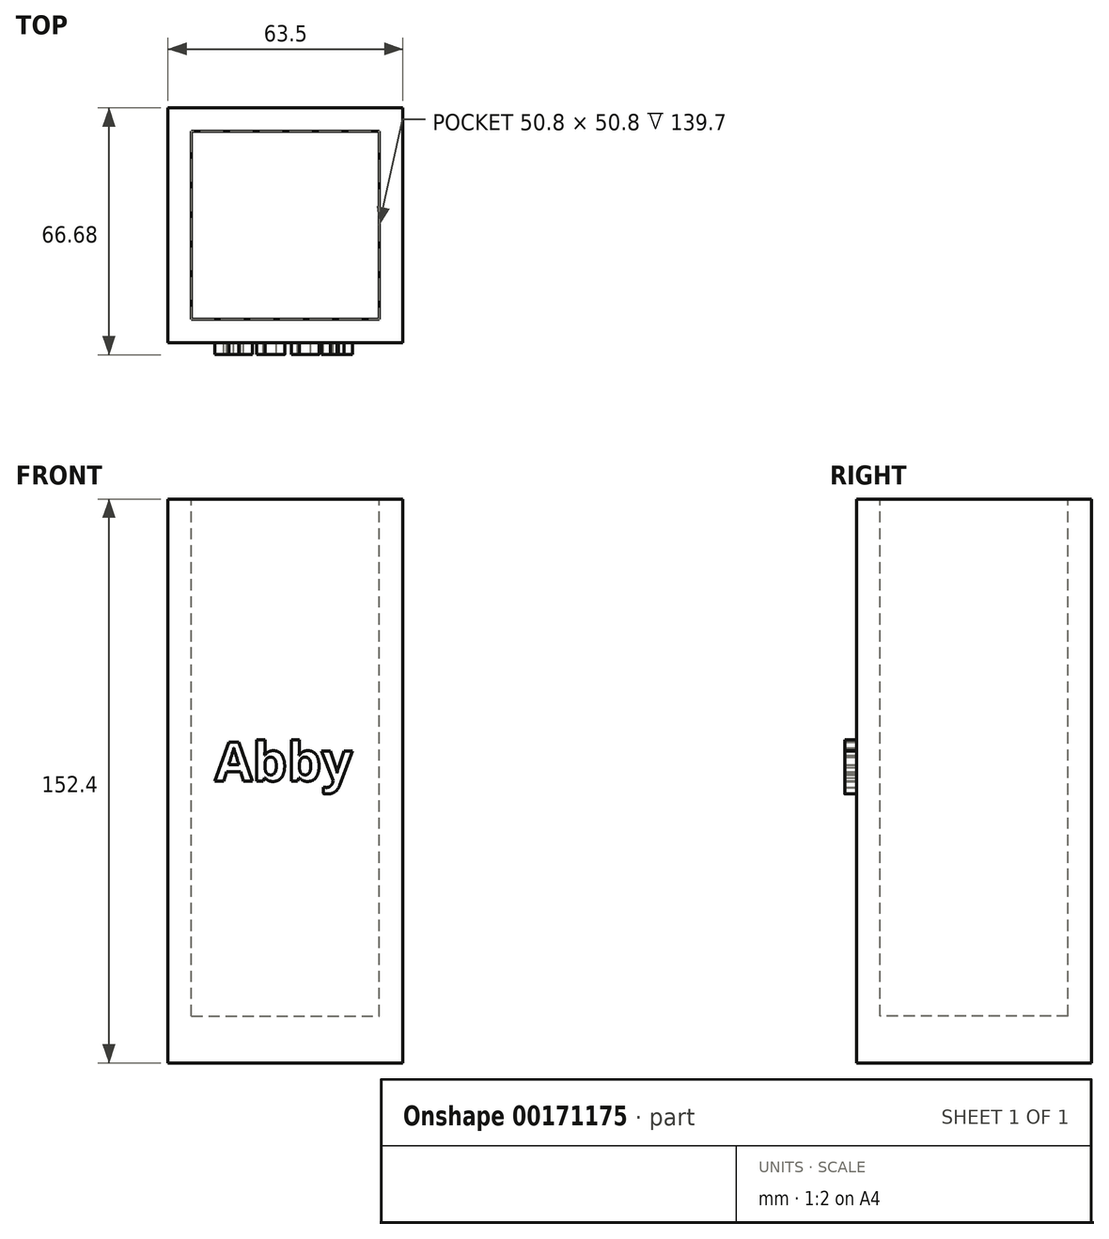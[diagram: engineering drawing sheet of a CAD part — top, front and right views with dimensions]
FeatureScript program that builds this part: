
annotation { "Feature Type Name" : "Feature", "Feature Type Description" : "" }
export const myFeature = defineFeature(function(context is Context, id is Id, definition is map)
    precondition{}
    {
        {
            var Q0;
            Q0=qCreatedBy(makeId("Front.planeOp"),FACE);
            var sketch = newSketch(context, id + "F0", { "sketchPlane" : qUnion([Q0])});
            skLineSegment(sketch, "E0.bottom", {"start": v(-32.8, 125.6) * mm, "end": v(30.7, 125.6) * mm});
            skLineSegment(sketch, "E0.top", {"start": v(-32.8, -26.8) * mm, "end": v(30.7, -26.8) * mm});
            skLineSegment(sketch, "E0.left", {"start": v(-32.8, 125.6) * mm, "end": v(-32.8, -26.8) * mm});
            skLineSegment(sketch, "E0.right", {"start": v(30.7, 125.6) * mm, "end": v(30.7, -26.8) * mm});
            skSolve(sketch);
        }
        {
            var Q0;
            Q0 = qSketchRegion(id + "F0", true);
            extrude(context, id + "F1", {"entities" : qUnion([Q0]), "depth" : 63.5 * mm});
        }
        {
            var Q0;
            Q0=makeQuery(id+"F1.opExtrude","SWEPT_FACE",FACE,{"disambiguationData":[OSD([sQuery(id+"F0.wireOp",EDGE,"E0.bottom")])]});
            var sketch = newSketch(context, id + "F2", { "sketchPlane" : qUnion([Q0])});
            skLineSegment(sketch, "E1.bottom", {"start": v(-26.44, -6.35) * mm, "end": v(24.36, -6.35) * mm});
            skLineSegment(sketch, "E1.top", {"start": v(-26.44, -57.15) * mm, "end": v(24.36, -57.15) * mm});
            skLineSegment(sketch, "E1.left", {"start": v(-26.44, -6.35) * mm, "end": v(-26.44, -57.15) * mm});
            skLineSegment(sketch, "E1.right", {"start": v(24.36, -6.35) * mm, "end": v(24.36, -57.15) * mm});
            skSolve(sketch);
        }
        {
            var Q0;
            Q0 = qSketchRegion(id + "F2", true);
            extrude(context, id + "F3", {"entities" : qUnion([Q0]), "operationType" : NewBodyOperationType.REMOVE, "oppositeDirection" : true, "depth" : 139.7 * mm});
        }
        {
            var Q0;
            Q0=makeQuery(id+"F1.opExtrude","CAP_FACE",FACE,{"disambiguationData":[OSD([sQuery(id+"F0.wireOp",EDGE,"E0.bottom"),sQuery(id+"F0.wireOp",EDGE,"E0.top"),sQuery(id+"F0.wireOp",EDGE,"E0.left"),sQuery(id+"F0.wireOp",EDGE,"E0.right")])],"isStart":false});
            var sketch = newSketch(context, id + "F4", { "sketchPlane" : qUnion([Q0])});
            skText(sketch, "E2", { "text": "Abby", "fontName": "OpenSans-Bold.ttf"});
            const initialGuessF4  = {"E2": [-0.0201, 0.0494, 1, 0, 0.0106]};
            skSetInitialGuess(sketch, initialGuessF4);
            skSolve(sketch);
        }
        {
            var Q0;
            Q0 = qSketchRegion(id + "F4", true);
            extrude(context, id + "F5", {"entities" : qUnion([Q0]), "operationType" : NewBodyOperationType.ADD, "depth" : 3.17 * mm});
        }
    });
